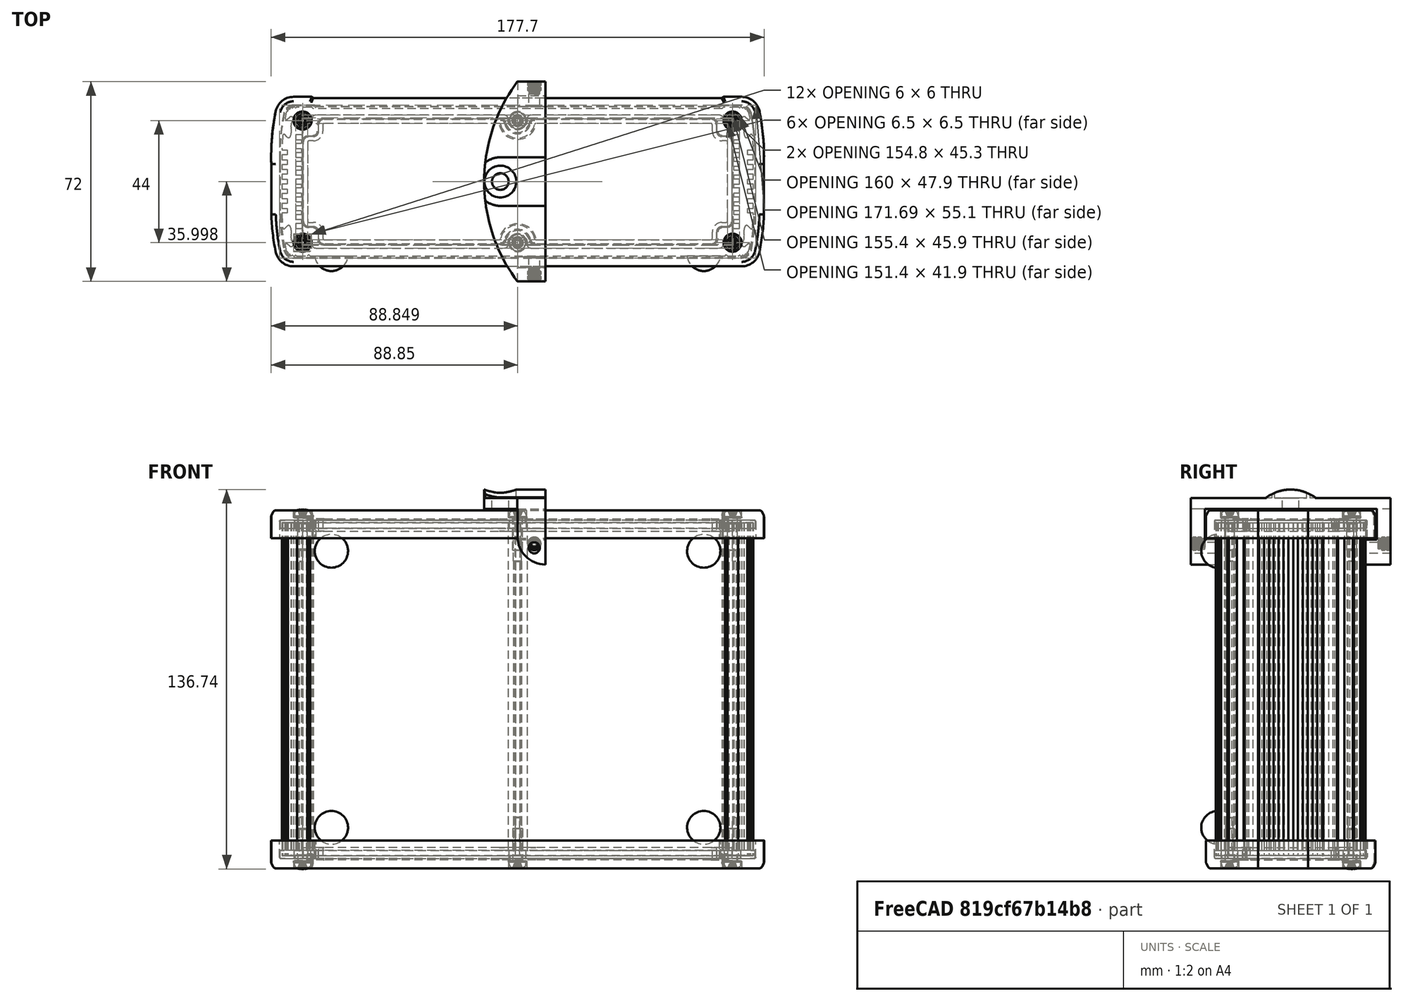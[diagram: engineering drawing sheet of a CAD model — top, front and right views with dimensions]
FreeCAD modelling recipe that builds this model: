
FCSTD DOCUMENT  (FreeCAD 0.20R29177 (Git))
Label: antennaHolder
License: All rights reserved
LicenseURL: http://en.wikipedia.org/wiki/All_rights_reserved
objects: Part::Cylinder×10, Part::Box×5, Part::MultiFuse×5, Part::Feature×3, Part::Cut×3, Part::MultiCommon×2
note: 28 computed .brp shape members not serialized (recipe doc carries the construction recipe); baked Part::Feature solids carry a one-line shape summary decoded from their .brp

FEATURE [Part::Feature] Feature  label="EX-64-002"
  shape: bbox 178.8 x 63.35 x 129.6 mm, 1628 faces, 33 solids (baked)
FEATURE [Part::Box] Box  label="out"
  AttacherType = Attacher::AttachEngine3D
  Height = 24
  Length = 10
  Placement = pos=(0,-36,45) rot=(0,0,1;0rad)
  Width = 72
FEATURE [Part::Box] Box001  label="in"
  AttacherType = Attacher::AttachEngine3D
  Height = 11
  Length = 10
  Placement = pos=(0,-31,54) rot=(0,0,1;0rad)
  Width = 62
FEATURE [Part::Box] Box002  label="in001"
  AttacherType = Attacher::AttachEngine3D
  Height = 11
  Length = 10
  Placement = pos=(0,-27,45) rot=(0,0,1;0rad)
  Width = 54
FEATURE [Part::MultiFuse] Fusion  label="in002"
  Shapes = -> [Box001,Box002]
FEATURE [Part::Cut] Cut
  Base = -> Box
  Tool = -> Fusion
FEATURE [Part::Feature] Solid  label="m3HeatSetInsert"
  Placement = pos=(6,31.5,52.5) rot=(0,0,1;0rad)
  shape: bbox 4.772 x 4.354 x 4.772 mm, 239 faces (baked)
FEATURE [Part::Cylinder] Cylinder
  Angle = 90
  AttacherType = Attacher::AttachEngine3D
  FirstAngle = 0
  Height = 5
  Placement = pos=(10,31,55) rot=(0.57735,-0.57735,-0.57735;4.18879rad)
  Radius = 10
  SecondAngle = 0
FEATURE [Part::Feature] Solid001  label="m3HeatSetInsert001"
  Placement = pos=(6,-31,52.5) rot=(0,0,1;3.14159rad)
  shape: bbox 4.772 x 4.354 x 4.772 mm, 239 faces (baked)
FEATURE [Part::Cylinder] Cylinder001
  Angle = 90
  AttacherType = Attacher::AttachEngine3D
  FirstAngle = 0
  Height = 5
  Placement = pos=(10,-31,55) rot=(0,0.707107,-0.707107;3.14159rad)
  Radius = 10
  SecondAngle = 0
FEATURE [Part::MultiFuse] Fusion001  label="out001"
  Shapes = -> [Cylinder,Cylinder001,Cut]
FEATURE [Part::Cylinder] Cylinder002
  Angle = 360
  AttacherType = Attacher::AttachEngine3D
  FirstAngle = 0
  Height = 4
  Placement = pos=(48,0,65) rot=(0,0,1;0rad)
  Radius = 60.06
  SecondAngle = 0
FEATURE [Part::Cylinder] Cylinder014  label="antennaIn001"
  Angle = 360
  AttacherType = Attacher::AttachEngine3D
  FirstAngle = 0
  Height = 10
  Placement = pos=(-6.23,0,69) rot=(0,0,1;0rad)
  Radius = 5.75
  SecondAngle = 0
FEATURE [Part::Cylinder] Cylinder013  label="antennaIn"
  Angle = 360
  AttacherType = Attacher::AttachEngine3D
  FirstAngle = 0
  Height = 10
  Placement = pos=(-6.23,0,65) rot=(0,0,1;0rad)
  Radius = 3
  SecondAngle = 0
FEATURE [Part::Cylinder] Cylinder015  label="antennaOut001"
  Angle = 360
  AttacherType = Attacher::AttachEngine3D
  FirstAngle = 0
  Height = 3
  Placement = pos=(-6.23,0,69) rot=(0,0,1;0rad)
  Radius = 8.75
  SecondAngle = 0
FEATURE [Part::Box] Box003  label="Cube"
  AttacherType = Attacher::AttachEngine3D
  Height = 3
  Length = 16.25
  Placement = pos=(-6.23,-8.75,69) rot=(0,0,1;0rad)
  Width = 17.5
FEATURE [Part::MultiFuse] Fusion002
  Shapes = -> [Fusion001,Cylinder002,Cylinder015,Box003]
FEATURE [Part::MultiFuse] Fusion003
  Shapes = -> [Cylinder013,Cylinder014]
FEATURE [Part::Cut] Cut001  label="base"
  Base = -> Fusion002
  Tool = -> Fusion003
FEATURE [Part::Cylinder] Cylinder016  label="m3HeastSetCut"
  Angle = 360
  AttacherType = Attacher::AttachEngine3D
  FirstAngle = 0
  Height = 94
  Placement = pos=(6,-47.35,51) rot=(1,0,0;4.71239rad)
  Radius = 2
  SecondAngle = 0
FEATURE [Part::Cut] Cut002
  Base = -> Cut001
  Tool = -> Cylinder016
FEATURE [Part::Cylinder] Cylinder017  label="include001"
  Angle = 90
  AttacherType = Attacher::AttachEngine3D
  FirstAngle = 0
  Height = 87
  Placement = pos=(10,-40.75,55) rot=(0.57735,-0.57735,-0.57735;4.18879rad)
  Radius = 10
  SecondAngle = 0
FEATURE [Part::Box] Box004  label="include"
  AttacherType = Attacher::AttachEngine3D
  Height = 14
  Length = 25
  Placement = pos=(-15,-36,55) rot=(0,0,1;0rad)
  Width = 72
FEATURE [Part::Cylinder] Cylinder018
  Angle = 360
  AttacherType = Attacher::AttachEngine3D
  FirstAngle = 0
  Height = 30
  Placement = pos=(-20,0,57) rot=(0.57735,0.57735,0.57735;2.0944rad)
  Radius = 15
  SecondAngle = 0
FEATURE [Part::MultiFuse] Fusion004  label="include002"
  Shapes = -> [Cylinder017,Box004,Cylinder018]
FEATURE [Part::MultiCommon] Common
  Shapes = -> [Fusion004,Cut002]
FEATURE [Part::Cylinder] Cylinder019
  Angle = 360
  AttacherType = Attacher::AttachEngine3D
  FirstAngle = 0
  Height = 44
  Placement = pos=(48,0,35.9) rot=(0,0,1;0rad)
  Radius = 60.06
  SecondAngle = 0
FEATURE [Part::MultiCommon] Common001
  Shapes = -> [Common,Cylinder019]
